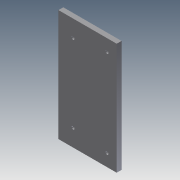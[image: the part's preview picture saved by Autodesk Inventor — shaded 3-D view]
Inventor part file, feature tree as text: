
AUTODESK INVENTOR PART (.ipt)
format: ipt  version: 2011 (Build 150239000, 239)  size: 147,968 bytes
history: native  units: in
note: dims shown in document units (in); Inventor stores cm internally (conversion verified against a paired STEP export)
features: extrude x9, sketch x9
ambient origin geometry x8: Origin, YZ Plane, XZ Plane, XY Plane, X Axis, Y Axis, Z Axis, Center Point
bodies: Solid1 (feature_tree)
feature tree (18):
  extrude  "Extrusion1"  Depth=6.0in
  extrude  "Extrusion2"  Depth=0.5in
  extrude  "Extrusion3"  Depth=0.5in
  extrude  "Extrusion4"  Depth=0.75in
  extrude  "Extrusion5"  Depth=0.75in
  extrude  "Extrusion6"  Depth=0.5in
  extrude  "Extrusion7"  Depth=0.156in
  extrude  "Extrusion8"  Depth=0.25in TaperAngle=0.0deg
  extrude  "Extrusion9"  Depth=5.5in
  sketch  "Sketch1"  dims[d0=2.9528in d1=6.0in]
  sketch  "Sketch2"  dims[d2=0.25in d3=0.0in d4=0.5in]
  sketch  "Sketch3"  dims[d5=1.0in d6=0.0in d7=0.5in]
  sketch  "Sketch4"  dims[d8=0.5in d9=0.75in]
  sketch  "Sketch5"  dims[d10=0.75in d11=0.75in]
  sketch  "Sketch6"  dims[d12=0.5in d13=0.5in]
  sketch  "Sketch7"  dims[d14=0.156in d15=0.156in]
  sketch  "Sketch8"  dims[d16=1.0in d17=0.0in d18=0.25in d19=0.0in]
  sketch  "Sketch9"  dims[d20=3.0in d21=0.0in d22=5.5in d23=0.1in d24=0.0in d25=0.5in d26=0.5in d27=0.5in d28=0.5in d29=0.156in d30=0.156in d31=1.0in d32=0.0in d33=0.125in d34=0.0in d35=0.125in d36=0.0in]
